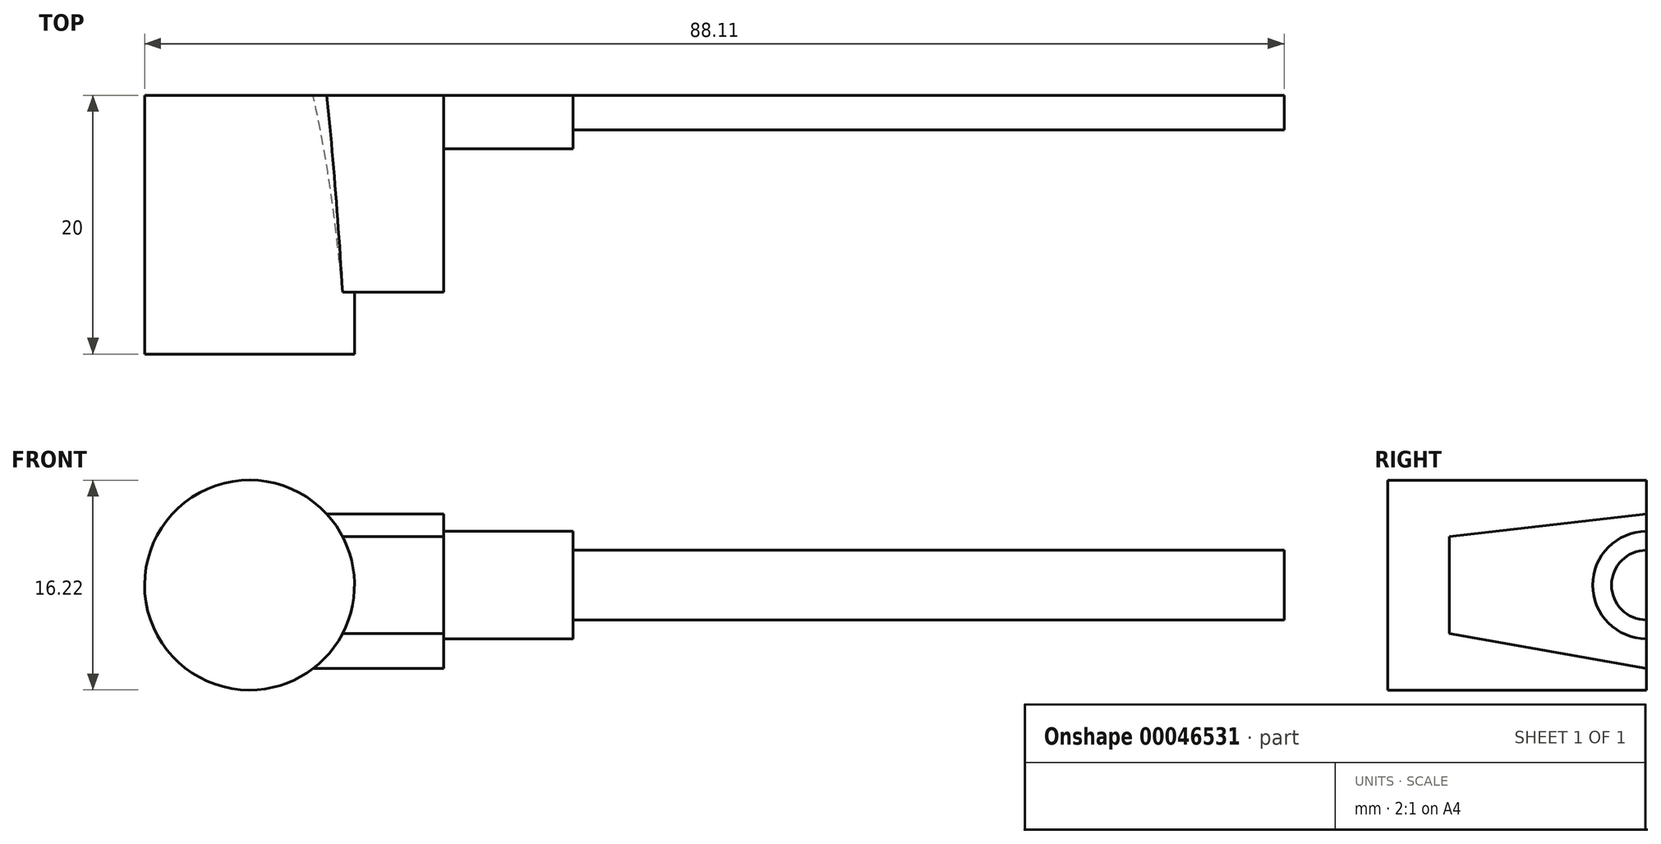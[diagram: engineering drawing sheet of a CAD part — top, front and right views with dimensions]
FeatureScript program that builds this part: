
annotation { "Feature Type Name" : "Feature", "Feature Type Description" : "" }
export const myFeature = defineFeature(function(context is Context, id is Id, definition is map)
    precondition{}
    {
        {
            var Q0;
            Q0=qCreatedBy(makeId("Front.planeOp"),FACE);
            var sketch = newSketch(context, id + "F0", { "sketchPlane" : qUnion([Q0])});
            skCircle(sketch, "E0", {"center": v(0, 0) * mm, "radius": 8.11 * mm});
            skSolve(sketch);
        }
        {
            var Q0;
            Q0=makeQuery(id+"F0.imprint","IMPRINT",FACE,{"disambiguationData":[TD([[makeQuery(id+"F0.imprint","IMPRINT",EDGE,{"derivedFrom":sQuery(id+"F0.wireOp",EDGE,"E0")}),1.0]])]});
            var Q1;
            Q1 = qSketchRegion(id + "FstWJH0pH44Twsx_1", true);
            extrude(context, id + "F1", {"entities" : qUnion([Q0, Q1]), "depth" : 20 * mm});
        }
        {
            var Q0;
            Q0=qCreatedBy(makeId("Right.planeOp"),FACE);
            var sketch = newSketch(context, id + "F2", { "sketchPlane" : qUnion([Q0])});
            skLineSegment(sketch, "E1", {"start": v(0, 5.5) * mm, "end": v(-15.23, 3.76) * mm});
            skLineSegment(sketch, "E2", {"start": v(-15.23, 3.76) * mm, "end": v(-15.23, -3.76) * mm});
            skLineSegment(sketch, "E3", {"start": v(-15.23, -3.76) * mm, "end": v(0, -6.46) * mm});
            skLineSegment(sketch, "E4", {"start": v(0, -6.46) * mm, "end": v(0, 5.5) * mm});
            skSolve(sketch);
        }
        {
            var Q0;
            Q0 = qSketchRegion(id + "F2", true);
            extrude(context, id + "F3", {"entities" : qUnion([Q0]), "operationType" : NewBodyOperationType.ADD, "depth" : 15 * mm});
        }
        {
            var Q0;
            Q0=qCreatedBy(makeId("Right.planeOp"),FACE);
            var sketch = newSketch(context, id + "F4", { "sketchPlane" : qUnion([Q0])});
            skArc(sketch, "E5", {"start": v(0, -4.14) * mm, "mid": v(-2.93, -2.93) * mm, "end": v(-4.14, 0) * mm});
            skArc(sketch, "E6", {"start": v(0, -4.14) * mm, "mid": v(-4.14, 0) * mm, "end": v(0, 4.14) * mm});
            skLineSegment(sketch, "E7", {"start": v(0, 4.14) * mm, "end": v(0, -4.14) * mm});
            skSolve(sketch);
        }
        {
            var Q0;
            Q0 = qSketchRegion(id + "F4", true);
            var Q1;
            Q1=sQuery(id+"F4.wireOp",EDGE,"E7");
            var Q2;
            Q2=sQuery(id+"F4.wireOp",EDGE,"E6");
            extrude(context, id + "F5", {"entities" : qUnion([Q0]), "operationType" : NewBodyOperationType.ADD, "surfaceEntities" : qUnion([Q1, Q2]), "depth" : 25 * mm});
        }
        {
            var Q0;
            Q0=qCreatedBy(makeId("Right.planeOp"),FACE);
            var sketch = newSketch(context, id + "F6", { "sketchPlane" : qUnion([Q0])});
            skArc(sketch, "E8", {"start": v(0, -2.7) * mm, "mid": v(-1.9, -1.9) * mm, "end": v(-2.7, 0) * mm});
            skArc(sketch, "E9", {"start": v(0, -2.7) * mm, "mid": v(-2.7, 0) * mm, "end": v(0, 2.7) * mm});
            skLineSegment(sketch, "E10", {"start": v(0, 2.7) * mm, "end": v(0, -2.7) * mm});
            skSolve(sketch);
        }
        {
            var Q0;
            Q0 = qSketchRegion(id + "F6", true);
            extrude(context, id + "F7", {"entities" : qUnion([Q0]), "operationType" : NewBodyOperationType.ADD, "depth" : 80 * mm});
        }
    });
